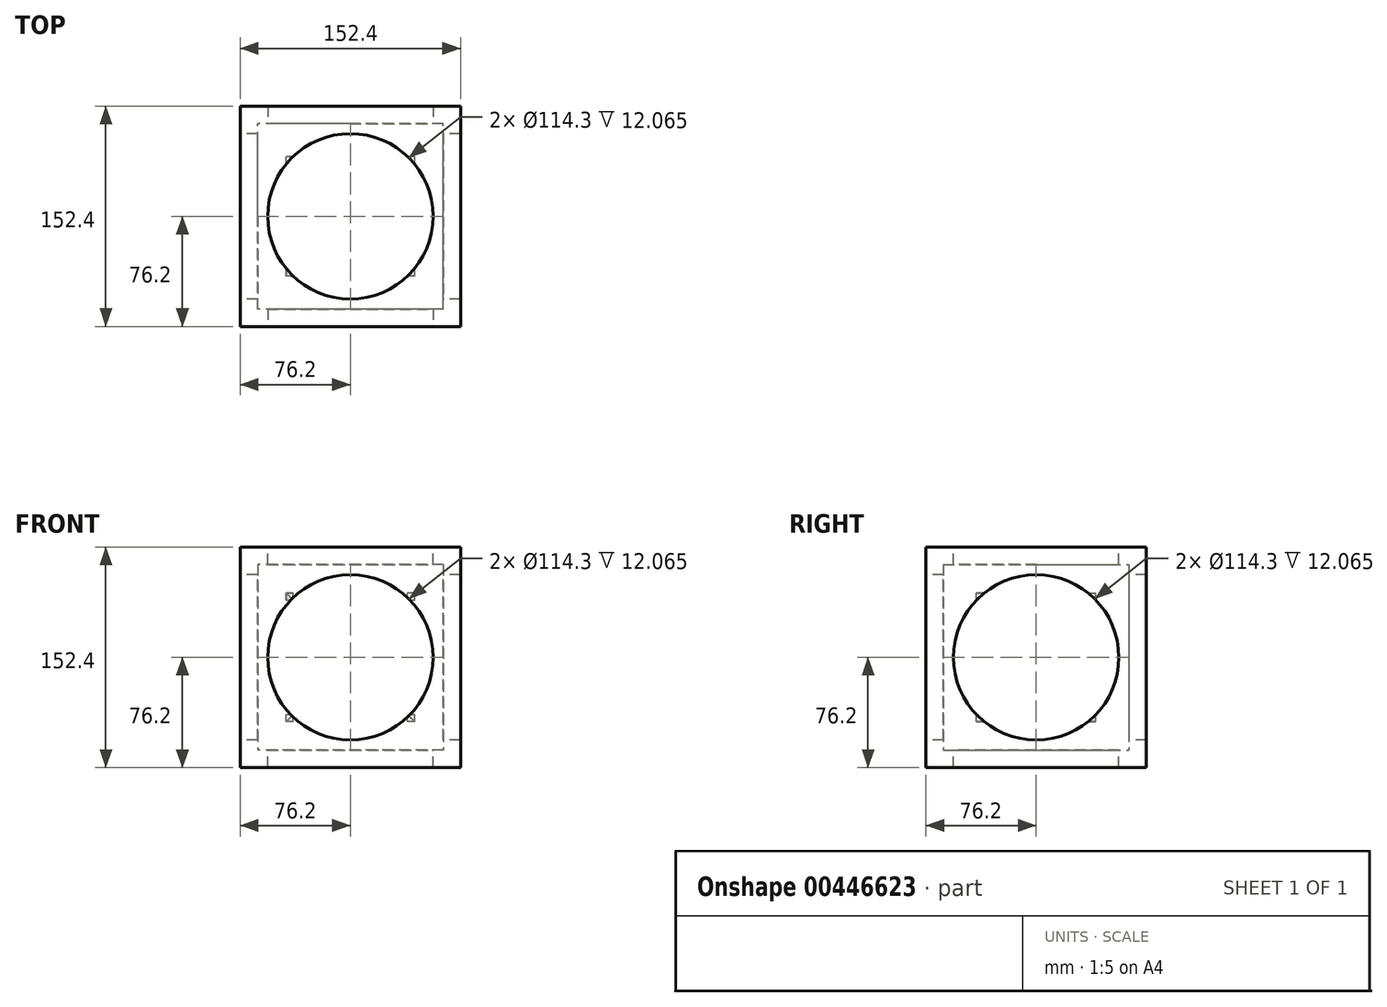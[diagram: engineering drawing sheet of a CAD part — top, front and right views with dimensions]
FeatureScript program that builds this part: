
annotation { "Feature Type Name" : "Feature", "Feature Type Description" : "" }
export const myFeature = defineFeature(function(context is Context, id is Id, definition is map)
    precondition{}
    {
        {
            var Q0;
            Q0=qCreatedBy(makeId("Front.planeOp"),FACE);
            var sketch = newSketch(context, id + "F0", { "sketchPlane" : qUnion([Q0])});
            skLineSegment(sketch, "E0.bottom", {"start": v(9.53, 9.53) * mm, "end": v(-9.53, 9.53) * mm});
            skLineSegment(sketch, "E0.top", {"start": v(9.53, -9.53) * mm, "end": v(-9.53, -9.53) * mm});
            skLineSegment(sketch, "E0.left", {"start": v(9.53, 9.53) * mm, "end": v(9.53, -9.53) * mm});
            skLineSegment(sketch, "E0.right", {"start": v(-9.53, 9.53) * mm, "end": v(-9.53, -9.53) * mm});
            skPoint(sketch, "E0.middle", {"position": v(0, 0) * mm});
            skSolve(sketch);
        }
        {
            var Q0;
            Q0 = qSketchRegion(id + "F0", true);
            extrude(context, id + "F1", {"entities" : qUnion([Q0]), "endBound" : BoundingType.SYMMETRIC, "depth" : 19.05 * mm});
        }
        {
            var Q0;
            Q0=qCreatedBy(makeId("Front.planeOp"),FACE);
            var sketch = newSketch(context, id + "F2", { "sketchPlane" : qUnion([Q0])});
            skLineSegment(sketch, "E1.bottom", {"start": v(15.88, 15.88) * mm, "end": v(-15.88, 15.88) * mm});
            skLineSegment(sketch, "E1.top", {"start": v(15.88, -15.88) * mm, "end": v(-15.88, -15.88) * mm});
            skLineSegment(sketch, "E1.left", {"start": v(15.88, 15.88) * mm, "end": v(15.88, -15.88) * mm});
            skLineSegment(sketch, "E1.right", {"start": v(-15.88, 15.88) * mm, "end": v(-15.88, -15.88) * mm});
            skPoint(sketch, "E1.middle", {"position": v(0, 0) * mm});
            skLineSegment(sketch, "E2.bottom", {"start": v(22.23, 22.23) * mm, "end": v(-22.23, 22.23) * mm});
            skLineSegment(sketch, "E2.top", {"start": v(22.23, -22.23) * mm, "end": v(-22.23, -22.23) * mm});
            skLineSegment(sketch, "E2.left", {"start": v(22.23, 22.23) * mm, "end": v(22.23, -22.23) * mm});
            skLineSegment(sketch, "E2.right", {"start": v(-22.23, 22.23) * mm, "end": v(-22.23, -22.23) * mm});
            skSolve(sketch);
        }
        {
            var Q0;
            Q0 = qSketchRegion(id + "F2", true);
            extrude(context, id + "F3", {"entities" : qUnion([Q0]), "endBound" : BoundingType.SYMMETRIC, "depth" : 44.45 * mm});
        }
        {
            var Q0;
            Q0=makeQuery(id+"F3.opExtrude","CAP_FACE",FACE,{"disambiguationData":[OSD([sQuery(id+"F2.wireOp",EDGE,"E1.bottom"),sQuery(id+"F2.wireOp",EDGE,"E1.top"),sQuery(id+"F2.wireOp",EDGE,"E1.left"),sQuery(id+"F2.wireOp",EDGE,"E1.right"),sQuery(id+"F2.wireOp",EDGE,"E2.bottom"),sQuery(id+"F2.wireOp",EDGE,"E2.top"),sQuery(id+"F2.wireOp",EDGE,"E2.left"),sQuery(id+"F2.wireOp",EDGE,"E2.right")])],"isStart":false});
            var sketch = newSketch(context, id + "F4", { "sketchPlane" : qUnion([Q0])});
            skLineSegment(sketch, "E3.0", {"start": v(-15.88, 15.88) * mm, "end": v(-15.88, -15.88) * mm});
            skLineSegment(sketch, "E4.0", {"start": v(15.88, 15.88) * mm, "end": v(-15.88, 15.88) * mm});
            skLineSegment(sketch, "E5.0", {"start": v(15.88, 15.88) * mm, "end": v(15.88, -15.88) * mm});
            skLineSegment(sketch, "E6.0", {"start": v(15.88, -15.88) * mm, "end": v(-15.88, -15.88) * mm});
            skSolve(sketch);
        }
        {
            var Q0;
            Q0 = qSketchRegion(id + "F4", true);
            extrude(context, id + "F5", {"entities" : qUnion([Q0]), "operationType" : NewBodyOperationType.ADD, "oppositeDirection" : true, "depth" : 6.35 * mm});
        }
        {
            var Q0;
            Q0=makeQuery(id+"F3.opExtrude","CAP_FACE",FACE,{"disambiguationData":[OSD([sQuery(id+"F2.wireOp",EDGE,"E1.bottom"),sQuery(id+"F2.wireOp",EDGE,"E1.top"),sQuery(id+"F2.wireOp",EDGE,"E1.left"),sQuery(id+"F2.wireOp",EDGE,"E1.right"),sQuery(id+"F2.wireOp",EDGE,"E2.bottom"),sQuery(id+"F2.wireOp",EDGE,"E2.top"),sQuery(id+"F2.wireOp",EDGE,"E2.left"),sQuery(id+"F2.wireOp",EDGE,"E2.right")])],"isStart":true});
            var sketch = newSketch(context, id + "F6", { "sketchPlane" : qUnion([Q0])});
            skLineSegment(sketch, "E7.0", {"start": v(-15.88, 15.88) * mm, "end": v(-15.88, -15.88) * mm});
            skLineSegment(sketch, "E8.0", {"start": v(-15.88, 15.88) * mm, "end": v(15.88, 15.88) * mm});
            skLineSegment(sketch, "E9.0", {"start": v(15.88, 15.88) * mm, "end": v(15.88, -15.88) * mm});
            skLineSegment(sketch, "E10.0", {"start": v(-15.88, -15.88) * mm, "end": v(15.88, -15.88) * mm});
            skSolve(sketch);
        }
        {
            var Q0;
            Q0 = qSketchRegion(id + "F6", true);
            extrude(context, id + "F7", {"entities" : qUnion([Q0]), "operationType" : NewBodyOperationType.ADD, "oppositeDirection" : true, "depth" : 6.35 * mm});
        }
        {
            var Q0;
            Q0=makeQuery(id+"F7.boolean.opBoolean","MERGE",FACE,{"derivedFrom":[makeQuery(id+"F3.opExtrude","CAP_FACE",FACE,{"disambiguationData":[OSD([sQuery(id+"F2.wireOp",EDGE,"E1.bottom"),sQuery(id+"F2.wireOp",EDGE,"E1.top"),sQuery(id+"F2.wireOp",EDGE,"E1.left"),sQuery(id+"F2.wireOp",EDGE,"E1.right"),sQuery(id+"F2.wireOp",EDGE,"E2.bottom"),sQuery(id+"F2.wireOp",EDGE,"E2.top"),sQuery(id+"F2.wireOp",EDGE,"E2.left"),sQuery(id+"F2.wireOp",EDGE,"E2.right")])],"isStart":true}),makeQuery(id+"F7.opExtrude","CAP_FACE",FACE,{"disambiguationData":[OSD([sQuery(id+"F6.wireOp",EDGE,"E7.0"),sQuery(id+"F6.wireOp",EDGE,"E8.0"),sQuery(id+"F6.wireOp",EDGE,"E9.0"),sQuery(id+"F6.wireOp",EDGE,"E10.0")])],"isStart":true})]});
            var sketch = newSketch(context, id + "F8", { "sketchPlane" : qUnion([Q0])});
            skCircle(sketch, "E11", {"center": v(0, 0) * mm, "radius": 11.9 * mm});
            skSolve(sketch);
        }
        {
            var Q0;
            Q0 = qSketchRegion(id + "F8", true);
            extrude(context, id + "F9", {"entities" : qUnion([Q0]), "operationType" : NewBodyOperationType.REMOVE, "endBound" : BoundingType.THROUGH_ALL, "oppositeDirection" : true, "depth" : 25.4 * mm});
        }
        {
            var Q0;
            Q0=makeQuery(id+"F3.opExtrude","SWEPT_FACE",FACE,{"disambiguationData":[OSD([sQuery(id+"F2.wireOp",EDGE,"E2.left")])]});
            var sketch = newSketch(context, id + "F10", { "sketchPlane" : qUnion([Q0])});
            skCircle(sketch, "E12", {"center": v(0, 0) * mm, "radius": 11.9 * mm});
            skSolve(sketch);
        }
        {
            var Q0;
            Q0 = qSketchRegion(id + "F10", true);
            extrude(context, id + "F11", {"entities" : qUnion([Q0]), "operationType" : NewBodyOperationType.REMOVE, "endBound" : BoundingType.THROUGH_ALL, "oppositeDirection" : true, "depth" : 25.4 * mm});
        }
        {
            var Q0;
            Q0=makeQuery(id+"F3.opExtrude","SWEPT_FACE",FACE,{"disambiguationData":[OSD([sQuery(id+"F2.wireOp",EDGE,"E2.top")])]});
            var sketch = newSketch(context, id + "F12", { "sketchPlane" : qUnion([Q0])});
            skCircle(sketch, "E13", {"center": v(0, 0) * mm, "radius": 11.9 * mm});
            skSolve(sketch);
        }
        {
            var Q0;
            Q0 = qSketchRegion(id + "F12", true);
            extrude(context, id + "F13", {"entities" : qUnion([Q0]), "operationType" : NewBodyOperationType.REMOVE, "endBound" : BoundingType.THROUGH_ALL, "oppositeDirection" : true, "depth" : 25.4 * mm});
        }
        {
            var Q0;
            Q0=qCreatedBy(makeId("Front.planeOp"),FACE);
            var sketch = newSketch(context, id + "F14", { "sketchPlane" : qUnion([Q0])});
            skLineSegment(sketch, "E14.bottom", {"start": v(33.34, 33.34) * mm, "end": v(-33.34, 33.34) * mm});
            skLineSegment(sketch, "E14.top", {"start": v(33.34, -33.34) * mm, "end": v(-33.34, -33.34) * mm});
            skLineSegment(sketch, "E14.left", {"start": v(33.34, 33.34) * mm, "end": v(33.34, -33.34) * mm});
            skLineSegment(sketch, "E14.right", {"start": v(-33.34, 33.34) * mm, "end": v(-33.34, -33.34) * mm});
            skPoint(sketch, "E14.middle", {"position": v(0, 0) * mm});
            skLineSegment(sketch, "E15.bottom", {"start": v(44.45, -44.45) * mm, "end": v(-44.45, -44.45) * mm});
            skLineSegment(sketch, "E15.top", {"start": v(44.45, 44.45) * mm, "end": v(-44.45, 44.45) * mm});
            skLineSegment(sketch, "E15.left", {"start": v(44.45, -44.45) * mm, "end": v(44.45, 44.45) * mm});
            skLineSegment(sketch, "E15.right", {"start": v(-44.45, -44.45) * mm, "end": v(-44.45, 44.45) * mm});
            skSolve(sketch);
        }
        {
            var Q0;
            Q0 = qSketchRegion(id + "F14", true);
            extrude(context, id + "F15", {"entities" : qUnion([Q0]), "endBound" : BoundingType.SYMMETRIC, "depth" : 82.55 * mm});
        }
        {
            var Q0;
            Q0=makeQuery(id+"F15.opExtrude","CAP_FACE",FACE,{"disambiguationData":[OSD([sQuery(id+"F14.wireOp",EDGE,"E14.bottom"),sQuery(id+"F14.wireOp",EDGE,"E14.top"),sQuery(id+"F14.wireOp",EDGE,"E14.left"),sQuery(id+"F14.wireOp",EDGE,"E14.right"),sQuery(id+"F14.wireOp",EDGE,"E15.bottom"),sQuery(id+"F14.wireOp",EDGE,"E15.top"),sQuery(id+"F14.wireOp",EDGE,"E15.left"),sQuery(id+"F14.wireOp",EDGE,"E15.right")])],"isStart":true});
            var sketch = newSketch(context, id + "F16", { "sketchPlane" : qUnion([Q0])});
            skLineSegment(sketch, "E16.0", {"start": v(-33.34, 33.34) * mm, "end": v(-33.34, -33.34) * mm});
            skLineSegment(sketch, "E16.1", {"start": v(-33.34, 33.34) * mm, "end": v(33.34, 33.34) * mm});
            skLineSegment(sketch, "E16.2", {"start": v(33.34, 33.34) * mm, "end": v(33.34, -33.34) * mm});
            skLineSegment(sketch, "E16.3", {"start": v(-33.34, -33.34) * mm, "end": v(33.34, -33.34) * mm});
            skSolve(sketch);
        }
        {
            var Q0;
            Q0 = qSketchRegion(id + "F16", true);
            extrude(context, id + "F17", {"entities" : qUnion([Q0]), "operationType" : NewBodyOperationType.ADD, "oppositeDirection" : true, "depth" : 9.52 * mm});
        }
        {
            var Q0;
            Q0=makeQuery(id+"F15.opExtrude","CAP_FACE",FACE,{"disambiguationData":[OSD([sQuery(id+"F14.wireOp",EDGE,"E14.bottom"),sQuery(id+"F14.wireOp",EDGE,"E14.top"),sQuery(id+"F14.wireOp",EDGE,"E14.left"),sQuery(id+"F14.wireOp",EDGE,"E14.right"),sQuery(id+"F14.wireOp",EDGE,"E15.bottom"),sQuery(id+"F14.wireOp",EDGE,"E15.top"),sQuery(id+"F14.wireOp",EDGE,"E15.left"),sQuery(id+"F14.wireOp",EDGE,"E15.right")])],"isStart":false});
            var sketch = newSketch(context, id + "F18", { "sketchPlane" : qUnion([Q0])});
            skLineSegment(sketch, "E17.0", {"start": v(-33.34, 33.34) * mm, "end": v(-33.34, -33.34) * mm});
            skLineSegment(sketch, "E17.1", {"start": v(33.34, 33.34) * mm, "end": v(-33.34, 33.34) * mm});
            skLineSegment(sketch, "E17.2", {"start": v(33.34, 33.34) * mm, "end": v(33.34, -33.34) * mm});
            skLineSegment(sketch, "E17.3", {"start": v(33.34, -33.34) * mm, "end": v(-33.34, -33.34) * mm});
            skSolve(sketch);
        }
        {
            var Q0;
            Q0 = qSketchRegion(id + "F18", true);
            extrude(context, id + "F19", {"entities" : qUnion([Q0]), "operationType" : NewBodyOperationType.ADD, "oppositeDirection" : true, "depth" : 9.52 * mm});
        }
        {
            var Q0;
            Q0=makeQuery(id+"F19.boolean.opBoolean","MERGE",FACE,{"derivedFrom":[makeQuery(id+"F15.opExtrude","CAP_FACE",FACE,{"disambiguationData":[OSD([sQuery(id+"F14.wireOp",EDGE,"E14.bottom"),sQuery(id+"F14.wireOp",EDGE,"E14.top"),sQuery(id+"F14.wireOp",EDGE,"E14.left"),sQuery(id+"F14.wireOp",EDGE,"E14.right"),sQuery(id+"F14.wireOp",EDGE,"E15.bottom"),sQuery(id+"F14.wireOp",EDGE,"E15.top"),sQuery(id+"F14.wireOp",EDGE,"E15.left"),sQuery(id+"F14.wireOp",EDGE,"E15.right")])],"isStart":false}),makeQuery(id+"F19.opExtrude","CAP_FACE",FACE,{"disambiguationData":[OSD([sQuery(id+"F18.wireOp",EDGE,"E17.0"),sQuery(id+"F18.wireOp",EDGE,"E17.1"),sQuery(id+"F18.wireOp",EDGE,"E17.2"),sQuery(id+"F18.wireOp",EDGE,"E17.3")])],"isStart":true})]});
            var sketch = newSketch(context, id + "F20", { "sketchPlane" : qUnion([Q0])});
            skCircle(sketch, "E18", {"center": v(0, 0) * mm, "radius": 28.58 * mm});
            skSolve(sketch);
        }
        {
            var Q0;
            Q0 = qSketchRegion(id + "F20", true);
            extrude(context, id + "F21", {"entities" : qUnion([Q0]), "operationType" : NewBodyOperationType.REMOVE, "endBound" : BoundingType.THROUGH_ALL, "oppositeDirection" : true, "depth" : 25.4 * mm});
        }
        {
            var Q0;
            Q0=makeQuery(id+"F15.opExtrude","SWEPT_FACE",FACE,{"disambiguationData":[OSD([sQuery(id+"F14.wireOp",EDGE,"E15.right")])]});
            var sketch = newSketch(context, id + "F22", { "sketchPlane" : qUnion([Q0])});
            skCircle(sketch, "E19", {"center": v(0, 0) * mm, "radius": 28.58 * mm});
            skSolve(sketch);
        }
        {
            var Q0;
            Q0 = qSketchRegion(id + "F22", true);
            extrude(context, id + "F23", {"entities" : qUnion([Q0]), "operationType" : NewBodyOperationType.REMOVE, "endBound" : BoundingType.THROUGH_ALL, "oppositeDirection" : true, "depth" : 25.4 * mm});
        }
        {
            var Q0;
            Q0=makeQuery(id+"F15.opExtrude","SWEPT_FACE",FACE,{"disambiguationData":[OSD([sQuery(id+"F14.wireOp",EDGE,"E15.top")])]});
            var sketch = newSketch(context, id + "F24", { "sketchPlane" : qUnion([Q0])});
            skCircle(sketch, "E20", {"center": v(0, 0) * mm, "radius": 28.58 * mm});
            skSolve(sketch);
        }
        {
            var Q0;
            Q0 = qSketchRegion(id + "F24", true);
            extrude(context, id + "F25", {"entities" : qUnion([Q0]), "operationType" : NewBodyOperationType.REMOVE, "endBound" : BoundingType.THROUGH_ALL, "oppositeDirection" : true, "depth" : 25.4 * mm});
        }
        {
            var Q0;
            Q0=qCreatedBy(makeId("Front.planeOp"),FACE);
            var sketch = newSketch(context, id + "F26", { "sketchPlane" : qUnion([Q0])});
            skLineSegment(sketch, "E21.bottom", {"start": v(64.14, 64.13) * mm, "end": v(-64.13, 64.13) * mm});
            skLineSegment(sketch, "E21.top", {"start": v(64.13, -64.13) * mm, "end": v(-64.14, -64.13) * mm});
            skLineSegment(sketch, "E21.left", {"start": v(64.13, 64.13) * mm, "end": v(64.13, -64.13) * mm});
            skLineSegment(sketch, "E21.right", {"start": v(-64.13, 64.13) * mm, "end": v(-64.13, -64.13) * mm});
            skPoint(sketch, "E21.middle", {"position": v(0, 0) * mm});
            skLineSegment(sketch, "E22.bottom", {"start": v(76.2, 76.2) * mm, "end": v(-76.2, 76.2) * mm});
            skLineSegment(sketch, "E22.top", {"start": v(76.2, -76.2) * mm, "end": v(-76.2, -76.2) * mm});
            skLineSegment(sketch, "E22.left", {"start": v(76.2, 76.2) * mm, "end": v(76.2, -76.2) * mm});
            skLineSegment(sketch, "E22.right", {"start": v(-76.2, 76.2) * mm, "end": v(-76.2, -76.2) * mm});
            skSolve(sketch);
        }
        {
            var Q0;
            Q0 = qSketchRegion(id + "F26", true);
            extrude(context, id + "F27", {"entities" : qUnion([Q0]), "endBound" : BoundingType.SYMMETRIC, "depth" : 152.4 * mm});
        }
        {
            var Q0;
            Q0=makeQuery(id+"F27.opExtrude","CAP_FACE",FACE,{"disambiguationData":[OSD([sQuery(id+"F26.wireOp",EDGE,"E21.bottom"),sQuery(id+"F26.wireOp",EDGE,"E21.top"),sQuery(id+"F26.wireOp",EDGE,"E21.left"),sQuery(id+"F26.wireOp",EDGE,"E21.right"),sQuery(id+"F26.wireOp",EDGE,"E22.bottom"),sQuery(id+"F26.wireOp",EDGE,"E22.top"),sQuery(id+"F26.wireOp",EDGE,"E22.left"),sQuery(id+"F26.wireOp",EDGE,"E22.right")])],"isStart":false});
            var sketch = newSketch(context, id + "F28", { "sketchPlane" : qUnion([Q0])});
            skLineSegment(sketch, "E23.0", {"start": v(-64.13, 64.13) * mm, "end": v(-64.13, -64.13) * mm});
            skLineSegment(sketch, "E23.1", {"start": v(64.14, 64.13) * mm, "end": v(-64.13, 64.13) * mm});
            skLineSegment(sketch, "E23.2", {"start": v(64.13, 64.13) * mm, "end": v(64.13, -64.13) * mm});
            skLineSegment(sketch, "E23.3", {"start": v(64.13, -64.13) * mm, "end": v(-64.13, -64.13) * mm});
            skSolve(sketch);
        }
        {
            var Q0;
            Q0 = qSketchRegion(id + "F28", true);
            extrude(context, id + "F29", {"entities" : qUnion([Q0]), "operationType" : NewBodyOperationType.ADD, "oppositeDirection" : true, "depth" : 12.06 * mm});
        }
        {
            var Q0;
            Q0=makeQuery(id+"F27.opExtrude","CAP_FACE",FACE,{"disambiguationData":[OSD([sQuery(id+"F26.wireOp",EDGE,"E21.bottom"),sQuery(id+"F26.wireOp",EDGE,"E21.top"),sQuery(id+"F26.wireOp",EDGE,"E21.left"),sQuery(id+"F26.wireOp",EDGE,"E21.right"),sQuery(id+"F26.wireOp",EDGE,"E22.bottom"),sQuery(id+"F26.wireOp",EDGE,"E22.top"),sQuery(id+"F26.wireOp",EDGE,"E22.left"),sQuery(id+"F26.wireOp",EDGE,"E22.right")])],"isStart":true});
            var sketch = newSketch(context, id + "F30", { "sketchPlane" : qUnion([Q0])});
            skLineSegment(sketch, "E24.0", {"start": v(-64.13, 64.13) * mm, "end": v(-64.13, -64.13) * mm});
            skLineSegment(sketch, "E24.1", {"start": v(-64.13, 64.13) * mm, "end": v(64.13, 64.13) * mm});
            skLineSegment(sketch, "E24.2", {"start": v(64.13, 64.13) * mm, "end": v(64.13, -64.13) * mm});
            skLineSegment(sketch, "E24.3", {"start": v(-64.13, -64.13) * mm, "end": v(64.13, -64.13) * mm});
            skSolve(sketch);
        }
        {
            var Q0;
            Q0 = qSketchRegion(id + "F30", true);
            extrude(context, id + "F31", {"entities" : qUnion([Q0]), "operationType" : NewBodyOperationType.ADD, "oppositeDirection" : true, "depth" : 12.06 * mm});
        }
        {
            var Q0;
            Q0=makeQuery(id+"F29.boolean.opBoolean","MERGE",FACE,{"derivedFrom":[makeQuery(id+"F27.opExtrude","CAP_FACE",FACE,{"disambiguationData":[OSD([sQuery(id+"F26.wireOp",EDGE,"E21.bottom"),sQuery(id+"F26.wireOp",EDGE,"E21.top"),sQuery(id+"F26.wireOp",EDGE,"E21.left"),sQuery(id+"F26.wireOp",EDGE,"E21.right"),sQuery(id+"F26.wireOp",EDGE,"E22.bottom"),sQuery(id+"F26.wireOp",EDGE,"E22.top"),sQuery(id+"F26.wireOp",EDGE,"E22.left"),sQuery(id+"F26.wireOp",EDGE,"E22.right")])],"isStart":false}),makeQuery(id+"F29.opExtrude","CAP_FACE",FACE,{"disambiguationData":[OSD([sQuery(id+"F28.wireOp",EDGE,"E23.0"),sQuery(id+"F28.wireOp",EDGE,"E23.1"),sQuery(id+"F28.wireOp",EDGE,"E23.2"),sQuery(id+"F28.wireOp",EDGE,"E23.3")])],"isStart":true})]});
            var sketch = newSketch(context, id + "F32", { "sketchPlane" : qUnion([Q0])});
            skCircle(sketch, "E25", {"center": v(0, 0) * mm, "radius": 57.15 * mm});
            skSolve(sketch);
        }
        {
            var Q0;
            Q0 = qSketchRegion(id + "F32", true);
            extrude(context, id + "F33", {"entities" : qUnion([Q0]), "operationType" : NewBodyOperationType.REMOVE, "endBound" : BoundingType.THROUGH_ALL, "oppositeDirection" : true, "depth" : 25.4 * mm});
        }
        {
            var Q0;
            Q0=makeQuery(id+"F27.opExtrude","SWEPT_FACE",FACE,{"disambiguationData":[OSD([sQuery(id+"F26.wireOp",EDGE,"E22.right")])]});
            var sketch = newSketch(context, id + "F34", { "sketchPlane" : qUnion([Q0])});
            skCircle(sketch, "E26", {"center": v(0, 0) * mm, "radius": 57.15 * mm});
            skSolve(sketch);
        }
        {
            var Q0;
            Q0=makeQuery(id+"F34.imprint","IMPRINT",FACE,{"disambiguationData":[TD([[makeQuery(id+"F34.imprint","IMPRINT",EDGE,{"derivedFrom":sQuery(id+"F34.wireOp",EDGE,"E26")}),1.0]])]});
            extrude(context, id + "F35", {"entities" : qUnion([Q0]), "operationType" : NewBodyOperationType.REMOVE, "endBound" : BoundingType.THROUGH_ALL, "oppositeDirection" : true, "depth" : 25.4 * mm});
        }
        {
            var Q0;
            Q0=makeQuery(id+"F27.opExtrude","SWEPT_FACE",FACE,{"disambiguationData":[OSD([sQuery(id+"F26.wireOp",EDGE,"E22.bottom")])]});
            var sketch = newSketch(context, id + "F36", { "sketchPlane" : qUnion([Q0])});
            skCircle(sketch, "E27", {"center": v(0, 0) * mm, "radius": 57.15 * mm});
            skSolve(sketch);
        }
        {
            var Q0;
            Q0 = qSketchRegion(id + "F36", true);
            extrude(context, id + "F37", {"entities" : qUnion([Q0]), "operationType" : NewBodyOperationType.REMOVE, "endBound" : BoundingType.THROUGH_ALL, "oppositeDirection" : true, "depth" : 25.4 * mm});
        }
    });
